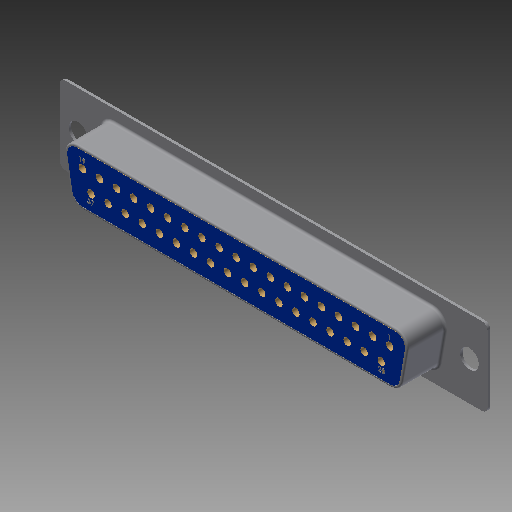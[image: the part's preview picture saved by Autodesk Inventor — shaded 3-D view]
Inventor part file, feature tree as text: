
AUTODESK INVENTOR PART (.ipt)
format: ipt  version: 2017 (Build 210142000, 142)  size: 432,128 bytes
history: native  units: in
note: dims shown in document units (in); Inventor stores cm internally (conversion verified against a paired STEP export)
features: extrude x1
ambient origin geometry x8: Origin, YZ Plane, XZ Plane, XY Plane, X Axis, Y Axis, Z Axis, Center Point
bodies: Solid1 (feature_tree)
feature tree (1):
  extrude  "Extrude11"  [1 undecoded]
note: 1 required parameter value undecoded (feature->parameter linkage not recoverable at this tier; creation-order binding heuristic only, values carry confidence <= 0.55)
